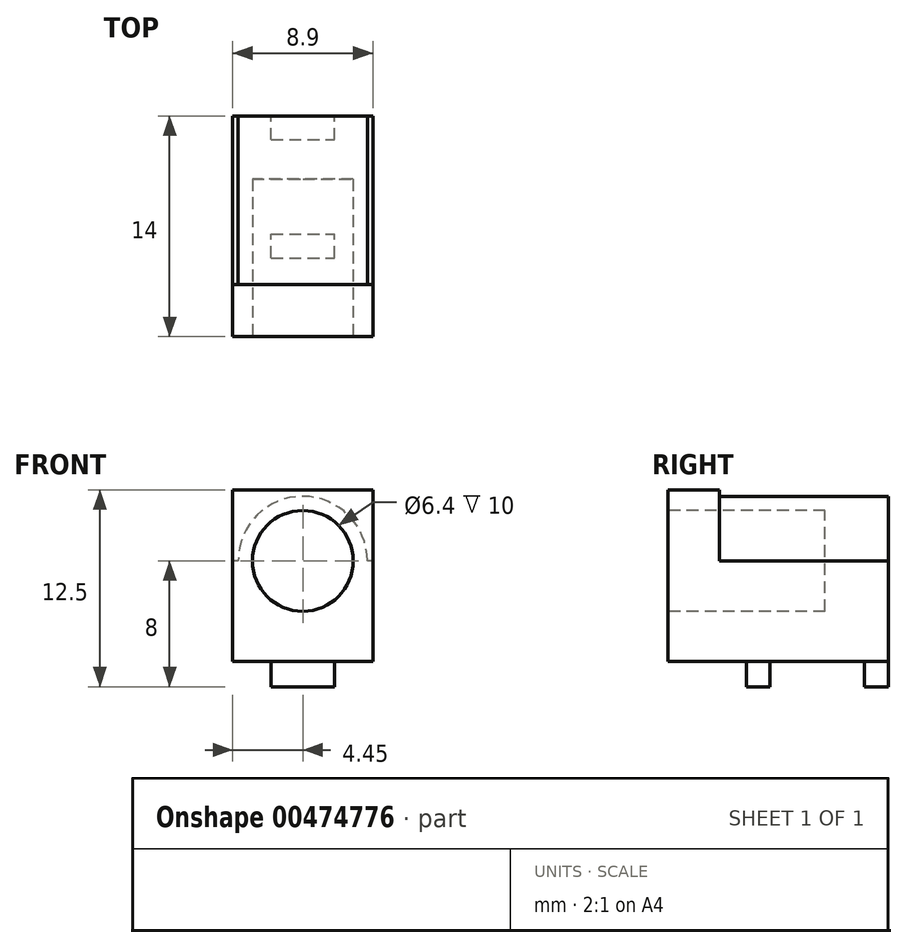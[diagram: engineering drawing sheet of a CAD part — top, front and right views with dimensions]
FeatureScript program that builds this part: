
annotation { "Feature Type Name" : "Feature", "Feature Type Description" : "" }
export const myFeature = defineFeature(function(context is Context, id is Id, definition is map)
    precondition{}
    {
        {
            var Q0;
            Q0=qCreatedBy(makeId("Front.planeOp"),FACE);
            var sketch = newSketch(context, id + "F0", { "sketchPlane" : qUnion([Q0])});
            skLineSegment(sketch, "E0.bottom", {"start": v(0, 0) * mm, "end": v(8.9, 0) * mm});
            skLineSegment(sketch, "E0.top", {"start": v(0, 10.9) * mm, "end": v(8.9, 10.9) * mm});
            skLineSegment(sketch, "E0.left", {"start": v(0, 0) * mm, "end": v(0, 10.9) * mm});
            skLineSegment(sketch, "E0.right", {"start": v(8.9, 0) * mm, "end": v(8.9, 10.9) * mm});
            skSolve(sketch);
        }
        {
            var Q0;
            Q0 = qSketchRegion(id + "F0", true);
            extrude(context, id + "F1", {"entities" : qUnion([Q0]), "depth" : 3.3 * mm});
        }
        {
            var Q0;
            Q0=makeQuery(id+"F1.opExtrude","CAP_FACE",FACE,{"disambiguationData":[OSD([sQuery(id+"F0.wireOp",EDGE,"E0.bottom"),sQuery(id+"F0.wireOp",EDGE,"E0.top"),sQuery(id+"F0.wireOp",EDGE,"E0.left"),sQuery(id+"F0.wireOp",EDGE,"E0.right")])],"isStart":true});
            var sketch = newSketch(context, id + "F2", { "sketchPlane" : qUnion([Q0])});
            skLineSegment(sketch, "E1", {"start": v(-8.9, 6.4) * mm, "end": v(-8.9, 0) * mm});
            skLineSegment(sketch, "E2", {"start": v(-8.9, 0) * mm, "end": v(0, 0) * mm});
            skLineSegment(sketch, "E3", {"start": v(0, 0) * mm, "end": v(0, 6.4) * mm});
            skLineSegment(sketch, "E4", {"start": v(0, 6.4) * mm, "end": v(-8.9, 6.4) * mm, "construction": true});
            skArc(sketch, "E5", {"start": v(-0.35, 6.4) * mm, "mid": v(-4.45, 10.5) * mm, "end": v(-8.55, 6.4) * mm});
            skLineSegment(sketch, "E6", {"start": v(-4.45, 10.9) * mm, "end": v(-4.45, 0) * mm, "construction": true});
            skLineSegment(sketch, "E7", {"start": v(-8.9, 6.4) * mm, "end": v(-8.55, 6.4) * mm});
            skLineSegment(sketch, "E8", {"start": v(-0.35, 6.4) * mm, "end": v(0, 6.4) * mm});
            skSolve(sketch);
        }
        {
            var Q0;
            Q0 = qSketchRegion(id + "F2", true);
            extrude(context, id + "F3", {"entities" : qUnion([Q0]), "operationType" : NewBodyOperationType.ADD, "depth" : 10.7 * mm});
        }
        {
            var Q0;
            Q0=makeQuery(id+"F1.opExtrude","CAP_FACE",FACE,{"disambiguationData":[OSD([sQuery(id+"F0.wireOp",EDGE,"E0.bottom"),sQuery(id+"F0.wireOp",EDGE,"E0.top"),sQuery(id+"F0.wireOp",EDGE,"E0.left"),sQuery(id+"F0.wireOp",EDGE,"E0.right")])],"isStart":false});
            var sketch = newSketch(context, id + "F4", { "sketchPlane" : qUnion([Q0])});
            skCircle(sketch, "E9", {"center": v(4.45, 6.4) * mm, "radius": 3.2 * mm});
            skSolve(sketch);
        }
        {
            var Q0;
            Q0 = qSketchRegion(id + "F4", true);
            extrude(context, id + "F5", {"entities" : qUnion([Q0]), "operationType" : NewBodyOperationType.REMOVE, "oppositeDirection" : true, "depth" : 10 * mm});
        }
        {
            var Q0;
            Q0=makeQuery(id+"F3.boolean.opBoolean","MERGE",FACE,{"derivedFrom":[makeQuery(id+"F1.opExtrude","SWEPT_FACE",FACE,{"disambiguationData":[OSD([sQuery(id+"F0.wireOp",EDGE,"E0.bottom")])]}),makeQuery(id+"F3.opExtrude","SWEPT_FACE",FACE,{"disambiguationData":[OSD([sQuery(id+"F2.wireOp",EDGE,"E2")])]})]});
            var sketch = newSketch(context, id + "F6", { "sketchPlane" : qUnion([Q0])});
            skLineSegment(sketch, "E10", {"start": v(4.45, 3.3) * mm, "end": v(4.45, -10.7) * mm, "construction": true});
            skLineSegment(sketch, "E11.bottom", {"start": v(2.45, -1.7) * mm, "end": v(6.45, -1.7) * mm});
            skLineSegment(sketch, "E11.top", {"start": v(2.45, -3.2) * mm, "end": v(6.45, -3.2) * mm});
            skLineSegment(sketch, "E11.left", {"start": v(2.45, -1.7) * mm, "end": v(2.45, -3.2) * mm});
            skLineSegment(sketch, "E11.right", {"start": v(6.45, -1.7) * mm, "end": v(6.45, -3.2) * mm});
            skLineSegment(sketch, "E12.bottom", {"start": v(2.45, -9.2) * mm, "end": v(6.45, -9.2) * mm});
            skLineSegment(sketch, "E12.top", {"start": v(2.45, -10.7) * mm, "end": v(6.45, -10.7) * mm});
            skLineSegment(sketch, "E12.left", {"start": v(2.45, -9.2) * mm, "end": v(2.45, -10.7) * mm});
            skLineSegment(sketch, "E12.right", {"start": v(6.45, -9.2) * mm, "end": v(6.45, -10.7) * mm});
            skSolve(sketch);
        }
        {
            var Q0;
            Q0 = qSketchRegion(id + "F6", true);
            extrude(context, id + "F7", {"entities" : qUnion([Q0]), "operationType" : NewBodyOperationType.ADD, "depth" : 1.6 * mm});
        }
    });
